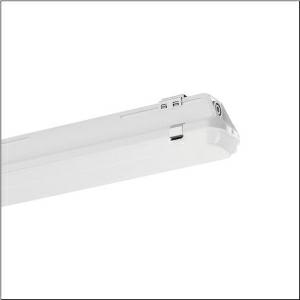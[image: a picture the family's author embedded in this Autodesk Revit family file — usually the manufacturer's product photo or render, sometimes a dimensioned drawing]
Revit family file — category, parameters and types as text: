
# Revit family: monsun_21_emergency_51fb207l447k3g
name_source: partatom
category: Lighting Fixtures
units: mm (PartAtom-declared; Revit-internal decimal feet)

## family parameters
Cut with Voids When Loaded = No
Host = Face
Light Source = No
Part Type = Normal
Room Calculation Point = No
Round Connector Dimension = Use Diameter
Shared = No

## types (1)
- --- (1 x LED, 820 lm, 7.1 W, 4000K)
    Apparent Load = 7 VA
    CIE Flux Codes = 45 75 93 94 100
    Color Rendering = 80
    Color Temperature = 4000K
    Default Elevation = 1800 mm
    Description = Monsun 21 emergency, damp-proof luminaire, chain hanger, primary optical cover: enclosure, of PC, light emission: direct distribution, primary light characteristic: symmetric, installation type: suspended mounting, surface-mounted, horizontal mounting, vertical mounting, LED, rated luminous flux: 4.320lm, luminous efficacy: 157lm/W, light colour: 840, colour temperature: 4000K, control gear: ON/OFF, with terminal, 3-pole, max. 2.5mm², mains connection: 220..240V, AC, 50/60Hz, rated input power: 31W, control gear: single battery element, battery: LiFePO4, 9Ah, housing, of glass-fibre reinforced plastic, uncoated, bright grey, incl. chain hanger, length: 1.299mm, width: 90mm, height: 88mm, clip for enclosure, of stainless steel (V2A), ceiling mounting element, of stainless steel (V2A), chain hanger, of stainless steel (V2A), protection rating (complete): IP66, insulation class (complete): insulation class I (protective earthing), certification: CE, UKCA, protection symbol: D, impact resistance: IK08, permissible operating ambient temperature: +5..+25°C, standard: EN 50419, EN 60598-2-1, corresponds to IFS (International Featured Standards) requirements for safety and quality in the food industry, for indoor or canopied outdoor use, no direct snow, no direct sun, no direct rain, LABS conformity tested according to VDMA 24364:2018-05, contact your sales advisor before using the luminaires in applications with unclear chemical exposure, large temperature fluctuations or condensation-forming humidity, packaging unit: 1 piece
    Height = 88 mm
    Lamp = 1 x LED
    Lamp Light Flux = 820 lm
    Lamp Power = 7.1 W
    Lamp count = 1
    Length = 1299 mm
    Luminous efficacy = 115 lm/W
    Manufacturer = Siteco
    ModVariant = No
    Model = 51FB207L447K3G
    Mounting Place = Ceiling
    Mounting Type = Surface mounted
    Number of Poles = 1
    OnlyDefault = Yes
    Power Factor = 1
    Product Name = Monsun 21 emergency
    Product group = damp-proof luminaire
    ProductGroupID = 300
    Protection Class = Protection class I
    Protection Degree = IP 66
    RLX_Detail_Level = 1
    RLX_Emergency_Light_Flux = 0 lm
    RLX_Emergency_Type = 0
    RLX_Emergency_Type_DB = No
    RlxData = <blob elided: 94045 chars, md5=2c7e5a7d>
    Socket = socket
    Standby Power = 0 W
    System Light Flux = 820 lm
    System Power = 7 W
    Type Comments = : 3 h
    Type Image = l_1319656.jpg
    URL = http://relux.com
    VarID = @adj_049549
    Voltage = 0 V
    Weight = 0.00 kg
    Width = 90 mm

## geometry (parser evidence)
native form markers: Blend x4, Sweep x13
no freeform markers — native parametric forms only
